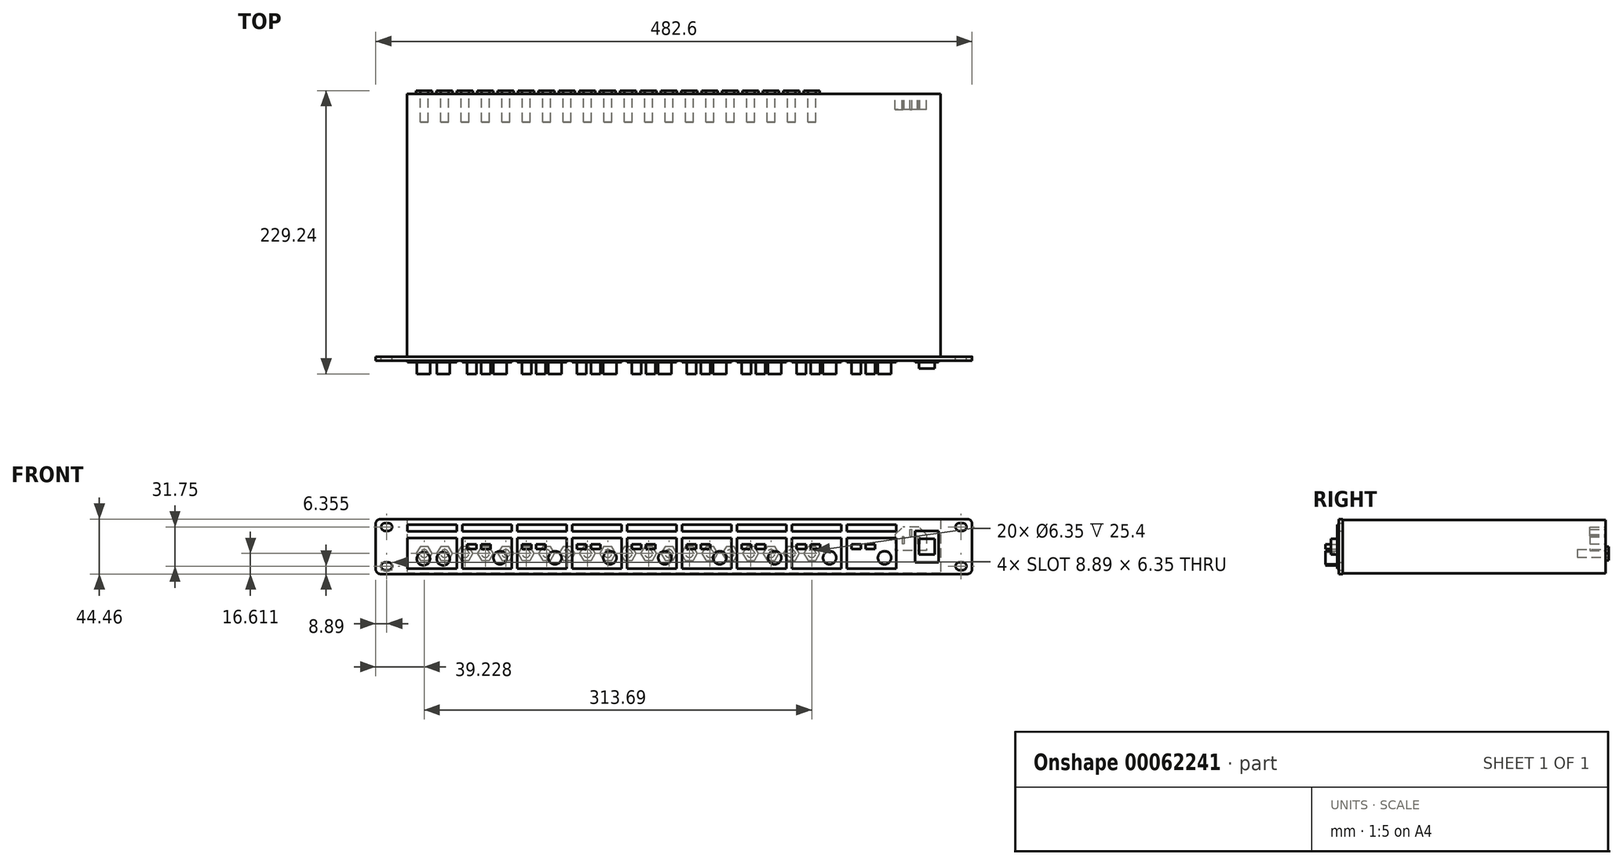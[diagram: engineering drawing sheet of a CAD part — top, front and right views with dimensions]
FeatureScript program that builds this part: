
annotation { "Feature Type Name" : "Feature", "Feature Type Description" : "" }
export const myFeature = defineFeature(function(context is Context, id is Id, definition is map)
    precondition{}
    {
        {
            var Q0;
            Q0=qCreatedBy(makeId("Front.planeOp"),FACE);
            var sketch = newSketch(context, id + "F0", { "sketchPlane" : qUnion([Q0])});
            skLineSegment(sketch, "E0.bottom", {"start": v(-237.5, 22.23) * mm, "end": v(237.5, 22.23) * mm});
            skLineSegment(sketch, "E0.top", {"start": v(-237.5, -22.22) * mm, "end": v(237.5, -22.22) * mm});
            skLineSegment(sketch, "E0.left", {"start": v(-241.3, 18.42) * mm, "end": v(-241.3, -18.41) * mm});
            skLineSegment(sketch, "E0.right", {"start": v(241.3, 18.42) * mm, "end": v(241.3, -18.42) * mm});
            skPoint(sketch, "E0.middle", {"position": v(0, 0) * mm});
            skArc(sketch, "E1", {"start": v(-233.68, 19.05) * mm, "mid": v(-236.86, 15.88) * mm, "end": v(-233.68, 12.7) * mm});
            skArc(sketch, "E2", {"start": v(-231.14, 12.7) * mm, "mid": v(-227.97, 15.88) * mm, "end": v(-231.14, 19.05) * mm});
            skLineSegment(sketch, "E3", {"start": v(-233.68, 12.7) * mm, "end": v(-231.14, 12.7) * mm});
            skLineSegment(sketch, "E4", {"start": v(-233.68, 19.05) * mm, "end": v(-231.14, 19.05) * mm});
            skPoint(sketch, "E5.visualSharp", {"position": v(-241.3, 22.23) * mm});
            skArc(sketch, "E5.filletArc", {"start": v(-237.5, 22.23) * mm, "mid": v(-240.18, 21.1) * mm, "end": v(-241.3, 18.42) * mm});
            skPoint(sketch, "E6.visualSharp", {"position": v(-241.3, -22.22) * mm});
            skArc(sketch, "E6.filletArc", {"start": v(-241.3, -18.41) * mm, "mid": v(-240.18, -21.1) * mm, "end": v(-237.5, -22.22) * mm});
            skPoint(sketch, "E7.visualSharp", {"position": v(241.3, 22.23) * mm});
            skArc(sketch, "E7.filletArc", {"start": v(241.3, 18.42) * mm, "mid": v(240.18, 21.1) * mm, "end": v(237.5, 22.23) * mm});
            skPoint(sketch, "E8.visualSharp", {"position": v(241.3, -22.22) * mm});
            skArc(sketch, "E8.filletArc", {"start": v(237.5, -22.23) * mm, "mid": v(240.18, -21.1) * mm, "end": v(241.3, -18.42) * mm});
            skLineSegment(sketch, "E9.MirrorCS", {"start": v(-233.68, -19.05) * mm, "end": v(-231.14, -19.05) * mm});
            skArc(sketch, "E10.MirrorCS", {"start": v(-231.14, -12.7) * mm, "mid": v(-227.97, -15.88) * mm, "end": v(-231.14, -19.05) * mm});
            skLineSegment(sketch, "E11.MirrorCS", {"start": v(-233.68, -12.7) * mm, "end": v(-231.14, -12.7) * mm});
            skArc(sketch, "E12.MirrorCS", {"start": v(-233.68, -19.05) * mm, "mid": v(-236.86, -15.88) * mm, "end": v(-233.68, -12.7) * mm});
            skLineSegment(sketch, "E13.MirrorCS", {"start": v(233.68, 12.7) * mm, "end": v(231.14, 12.7) * mm});
            skLineSegment(sketch, "E14.MirrorCS", {"start": v(233.68, -12.7) * mm, "end": v(231.14, -12.7) * mm});
            skLineSegment(sketch, "E15.MirrorCS", {"start": v(233.68, 19.05) * mm, "end": v(231.14, 19.05) * mm});
            skLineSegment(sketch, "E16.MirrorCS", {"start": v(233.68, -19.05) * mm, "end": v(231.14, -19.05) * mm});
            skArc(sketch, "E17.MirrorCS", {"start": v(233.68, -19.05) * mm, "mid": v(236.86, -15.88) * mm, "end": v(233.68, -12.7) * mm});
            skArc(sketch, "E18.MirrorCS", {"start": v(231.14, 12.7) * mm, "mid": v(227.97, 15.88) * mm, "end": v(231.14, 19.05) * mm});
            skArc(sketch, "E19.MirrorCS", {"start": v(233.68, 19.05) * mm, "mid": v(236.86, 15.88) * mm, "end": v(233.68, 12.7) * mm});
            skArc(sketch, "E20.MirrorCS", {"start": v(231.14, -12.7) * mm, "mid": v(227.97, -15.88) * mm, "end": v(231.14, -19.05) * mm});
            skSolve(sketch);
        }
        {
            var Q0;
            Q0=qSketchRegion(id+"F0",true);
            extrude(context, id + "F1", {"entities" : qUnion([Q0]), "depth" : 3.17 * mm});
        }
        {
            var Q0;
            Q0=makeQuery(id+"F1.opExtrude","CAP_FACE",FACE,{"disambiguationData":[OSD([sQuery(id+"F0.wireOp",EDGE,"E0.bottom"),sQuery(id+"F0.wireOp",EDGE,"E0.top"),sQuery(id+"F0.wireOp",EDGE,"E0.left"),sQuery(id+"F0.wireOp",EDGE,"E0.right"),sQuery(id+"F0.wireOp",EDGE,"E1"),sQuery(id+"F0.wireOp",EDGE,"E2"),sQuery(id+"F0.wireOp",EDGE,"E3"),sQuery(id+"F0.wireOp",EDGE,"E4"),sQuery(id+"F0.wireOp",EDGE,"E5.filletArc"),sQuery(id+"F0.wireOp",EDGE,"E6.filletArc"),sQuery(id+"F0.wireOp",EDGE,"E7.filletArc"),sQuery(id+"F0.wireOp",EDGE,"E8.filletArc"),sQuery(id+"F0.wireOp",EDGE,"E9.MirrorCS"),sQuery(id+"F0.wireOp",EDGE,"E10.MirrorCS"),sQuery(id+"F0.wireOp",EDGE,"E11.MirrorCS"),sQuery(id+"F0.wireOp",EDGE,"E12.MirrorCS"),sQuery(id+"F0.wireOp",EDGE,"E13.MirrorCS"),sQuery(id+"F0.wireOp",EDGE,"E14.MirrorCS"),sQuery(id+"F0.wireOp",EDGE,"E15.MirrorCS"),sQuery(id+"F0.wireOp",EDGE,"E16.MirrorCS"),sQuery(id+"F0.wireOp",EDGE,"E17.MirrorCS"),sQuery(id+"F0.wireOp",EDGE,"E18.MirrorCS"),sQuery(id+"F0.wireOp",EDGE,"E19.MirrorCS"),sQuery(id+"F0.wireOp",EDGE,"E20.MirrorCS")])],"isStart":true});
            var sketch = newSketch(context, id + "F2", { "sketchPlane" : qUnion([Q0])});
            skLineSegment(sketch, "E21.bottom", {"start": v(-215.9, 21.59) * mm, "end": v(215.9, 21.59) * mm});
            skLineSegment(sketch, "E21.top", {"start": v(-215.9, -21.6) * mm, "end": v(215.9, -21.6) * mm});
            skLineSegment(sketch, "E21.left", {"start": v(-215.9, 21.59) * mm, "end": v(-215.9, -21.6) * mm});
            skLineSegment(sketch, "E21.right", {"start": v(215.9, 21.59) * mm, "end": v(215.9, -21.6) * mm});
            skPoint(sketch, "E21.middle", {"position": v(0, 0) * mm});
            skSolve(sketch);
        }
        {
            var Q0;
            Q0 = qSketchRegion(id + "F2", true);
            extrude(context, id + "F3", {"entities" : qUnion([Q0]), "operationType" : NewBodyOperationType.ADD, "depth" : 212.72 * mm});
        }
        {
            var Q0;
            Q0=makeQuery(id+"F3.opExtrude","CAP_FACE",FACE,{"disambiguationData":[OSD([sQuery(id+"F2.wireOp",EDGE,"E21.bottom"),sQuery(id+"F2.wireOp",EDGE,"E21.top"),sQuery(id+"F2.wireOp",EDGE,"E21.left"),sQuery(id+"F2.wireOp",EDGE,"E21.right")])],"isStart":false});
            var sketch = newSketch(context, id + "F4", { "sketchPlane" : qUnion([Q0])});
            skCircle(sketch, "E22.cCircle", {"center": v(-111.62, -5.62) * mm, "radius": 5.62 * mm, "construction": true});
            skLineSegment(sketch, "E22.0", {"start": v(-114.86, 0) * mm, "end": v(-108.37, 0) * mm});
            skLineSegment(sketch, "E22.1", {"start": v(-108.37, 0) * mm, "end": v(-105.13, -5.62) * mm});
            skLineSegment(sketch, "E22.2", {"start": v(-105.13, -5.62) * mm, "end": v(-108.37, -11.24) * mm});
            skLineSegment(sketch, "E22.3", {"start": v(-108.37, -11.24) * mm, "end": v(-114.86, -11.24) * mm});
            skLineSegment(sketch, "E22.4", {"start": v(-114.86, -11.24) * mm, "end": v(-118.1, -5.62) * mm});
            skLineSegment(sketch, "E22.5", {"start": v(-118.1, -5.62) * mm, "end": v(-114.86, 0) * mm});
            skPoint(sketch, "E22.0.midPoint", {"position": v(-111.62, 0) * mm});
            skLineSegment(sketch, "E23.1.0.0", {"start": v(-88.62, -5.62) * mm, "end": v(-91.86, -11.24) * mm});
            skLineSegment(sketch, "E23.1.0.1", {"start": v(-91.86, 0) * mm, "end": v(-88.62, -5.62) * mm});
            skLineSegment(sketch, "E23.1.0.2", {"start": v(-98.35, 0) * mm, "end": v(-91.86, 0) * mm});
            skCircle(sketch, "E23.1.0.3", {"center": v(-95.1, -5.62) * mm, "radius": 5.62 * mm, "construction": true});
            skPoint(sketch, "E23.1.0.4", {"position": v(-95.1, 0) * mm});
            skLineSegment(sketch, "E23.1.0.5", {"start": v(-101.6, -5.62) * mm, "end": v(-98.35, 0) * mm});
            skLineSegment(sketch, "E23.1.0.6", {"start": v(-98.35, -11.24) * mm, "end": v(-101.6, -5.62) * mm});
            skLineSegment(sketch, "E23.1.0.7", {"start": v(-91.86, -11.24) * mm, "end": v(-98.35, -11.24) * mm});
            skLineSegment(sketch, "E23.2.0.0", {"start": v(-72.1, -5.62) * mm, "end": v(-75.35, -11.24) * mm});
            skLineSegment(sketch, "E23.2.0.1", {"start": v(-75.35, 0) * mm, "end": v(-72.1, -5.62) * mm});
            skLineSegment(sketch, "E23.2.0.2", {"start": v(-81.84, 0) * mm, "end": v(-75.35, 0) * mm});
            skCircle(sketch, "E23.2.0.3", {"center": v(-78.6, -5.62) * mm, "radius": 5.62 * mm, "construction": true});
            skPoint(sketch, "E23.2.0.4", {"position": v(-78.6, 0) * mm});
            skLineSegment(sketch, "E23.2.0.5", {"start": v(-85.09, -5.62) * mm, "end": v(-81.84, 0) * mm});
            skLineSegment(sketch, "E23.2.0.6", {"start": v(-81.84, -11.24) * mm, "end": v(-85.09, -5.62) * mm});
            skLineSegment(sketch, "E23.2.0.7", {"start": v(-75.35, -11.24) * mm, "end": v(-81.84, -11.24) * mm});
            skLineSegment(sketch, "E23.3.0.0", {"start": v(-55.6, -5.62) * mm, "end": v(-58.84, -11.24) * mm});
            skLineSegment(sketch, "E23.3.0.1", {"start": v(-58.84, 0) * mm, "end": v(-55.6, -5.62) * mm});
            skLineSegment(sketch, "E23.3.0.2", {"start": v(-65.33, 0) * mm, "end": v(-58.84, 0) * mm});
            skCircle(sketch, "E23.3.0.3", {"center": v(-62.09, -5.62) * mm, "radius": 5.62 * mm, "construction": true});
            skPoint(sketch, "E23.3.0.4", {"position": v(-62.09, 0) * mm});
            skLineSegment(sketch, "E23.3.0.5", {"start": v(-68.58, -5.62) * mm, "end": v(-65.33, 0) * mm});
            skLineSegment(sketch, "E23.3.0.6", {"start": v(-65.33, -11.24) * mm, "end": v(-68.58, -5.62) * mm});
            skLineSegment(sketch, "E23.3.0.7", {"start": v(-58.84, -11.24) * mm, "end": v(-65.33, -11.24) * mm});
            skLineSegment(sketch, "E23.4.0.0", {"start": v(-39.09, -5.62) * mm, "end": v(-42.33, -11.24) * mm});
            skLineSegment(sketch, "E23.4.0.1", {"start": v(-42.33, 0) * mm, "end": v(-39.09, -5.62) * mm});
            skLineSegment(sketch, "E23.4.0.2", {"start": v(-48.82, 0) * mm, "end": v(-42.33, 0) * mm});
            skCircle(sketch, "E23.4.0.3", {"center": v(-45.58, -5.62) * mm, "radius": 5.62 * mm, "construction": true});
            skPoint(sketch, "E23.4.0.4", {"position": v(-45.58, 0) * mm});
            skLineSegment(sketch, "E23.4.0.5", {"start": v(-52.07, -5.62) * mm, "end": v(-48.82, 0) * mm});
            skLineSegment(sketch, "E23.4.0.6", {"start": v(-48.82, -11.24) * mm, "end": v(-52.07, -5.62) * mm});
            skLineSegment(sketch, "E23.4.0.7", {"start": v(-42.33, -11.24) * mm, "end": v(-48.82, -11.24) * mm});
            skLineSegment(sketch, "E23.5.0.0", {"start": v(-22.58, -5.62) * mm, "end": v(-25.82, -11.24) * mm});
            skLineSegment(sketch, "E23.5.0.1", {"start": v(-25.82, 0) * mm, "end": v(-22.58, -5.62) * mm});
            skLineSegment(sketch, "E23.5.0.2", {"start": v(-32.31, 0) * mm, "end": v(-25.82, 0) * mm});
            skCircle(sketch, "E23.5.0.3", {"center": v(-29.07, -5.62) * mm, "radius": 5.62 * mm, "construction": true});
            skPoint(sketch, "E23.5.0.4", {"position": v(-29.07, 0) * mm});
            skLineSegment(sketch, "E23.5.0.5", {"start": v(-35.56, -5.62) * mm, "end": v(-32.31, 0) * mm});
            skLineSegment(sketch, "E23.5.0.6", {"start": v(-32.31, -11.24) * mm, "end": v(-35.56, -5.62) * mm});
            skLineSegment(sketch, "E23.5.0.7", {"start": v(-25.82, -11.24) * mm, "end": v(-32.31, -11.24) * mm});
            skLineSegment(sketch, "E23.6.0.0", {"start": v(-6.07, -5.62) * mm, "end": v(-9.31, -11.24) * mm});
            skLineSegment(sketch, "E23.6.0.1", {"start": v(-9.31, 0) * mm, "end": v(-6.07, -5.62) * mm});
            skLineSegment(sketch, "E23.6.0.2", {"start": v(-15.8, 0) * mm, "end": v(-9.31, 0) * mm});
            skCircle(sketch, "E23.6.0.3", {"center": v(-12.56, -5.62) * mm, "radius": 5.62 * mm, "construction": true});
            skPoint(sketch, "E23.6.0.4", {"position": v(-12.56, 0) * mm});
            skLineSegment(sketch, "E23.6.0.5", {"start": v(-19.05, -5.62) * mm, "end": v(-15.8, 0) * mm});
            skLineSegment(sketch, "E23.6.0.6", {"start": v(-15.8, -11.24) * mm, "end": v(-19.05, -5.62) * mm});
            skLineSegment(sketch, "E23.6.0.7", {"start": v(-9.31, -11.24) * mm, "end": v(-15.8, -11.24) * mm});
            skLineSegment(sketch, "E23.7.0.0", {"start": v(10.44, -5.62) * mm, "end": v(7.2, -11.24) * mm});
            skLineSegment(sketch, "E23.7.0.1", {"start": v(7.2, 0) * mm, "end": v(10.44, -5.62) * mm});
            skLineSegment(sketch, "E23.7.0.2", {"start": v(0.7, 0) * mm, "end": v(7.2, 0) * mm});
            skCircle(sketch, "E23.7.0.3", {"center": v(3.95, -5.62) * mm, "radius": 5.62 * mm, "construction": true});
            skPoint(sketch, "E23.7.0.4", {"position": v(3.95, 0) * mm});
            skLineSegment(sketch, "E23.7.0.5", {"start": v(-2.54, -5.62) * mm, "end": v(0.7, 0) * mm});
            skLineSegment(sketch, "E23.7.0.6", {"start": v(0.7, -11.24) * mm, "end": v(-2.54, -5.62) * mm});
            skLineSegment(sketch, "E23.7.0.7", {"start": v(7.2, -11.24) * mm, "end": v(0.7, -11.24) * mm});
            skLineSegment(sketch, "E23.8.0.0", {"start": v(26.95, -5.62) * mm, "end": v(23.7, -11.24) * mm});
            skLineSegment(sketch, "E23.8.0.1", {"start": v(23.7, 0) * mm, "end": v(26.95, -5.62) * mm});
            skLineSegment(sketch, "E23.8.0.2", {"start": v(17.22, 0) * mm, "end": v(23.7, 0) * mm});
            skCircle(sketch, "E23.8.0.3", {"center": v(20.46, -5.62) * mm, "radius": 5.62 * mm, "construction": true});
            skPoint(sketch, "E23.8.0.4", {"position": v(20.46, 0) * mm});
            skLineSegment(sketch, "E23.8.0.5", {"start": v(13.97, -5.62) * mm, "end": v(17.22, 0) * mm});
            skLineSegment(sketch, "E23.8.0.6", {"start": v(17.22, -11.24) * mm, "end": v(13.97, -5.62) * mm});
            skLineSegment(sketch, "E23.8.0.7", {"start": v(23.7, -11.24) * mm, "end": v(17.22, -11.24) * mm});
            skLineSegment(sketch, "E23.9.0.0", {"start": v(43.46, -5.62) * mm, "end": v(40.22, -11.24) * mm});
            skLineSegment(sketch, "E23.9.0.1", {"start": v(40.22, 0) * mm, "end": v(43.46, -5.62) * mm});
            skLineSegment(sketch, "E23.9.0.2", {"start": v(33.73, 0) * mm, "end": v(40.22, 0) * mm});
            skCircle(sketch, "E23.9.0.3", {"center": v(36.97, -5.62) * mm, "radius": 5.62 * mm, "construction": true});
            skPoint(sketch, "E23.9.0.4", {"position": v(36.97, 0) * mm});
            skLineSegment(sketch, "E23.9.0.5", {"start": v(30.48, -5.62) * mm, "end": v(33.73, 0) * mm});
            skLineSegment(sketch, "E23.9.0.6", {"start": v(33.73, -11.24) * mm, "end": v(30.48, -5.62) * mm});
            skLineSegment(sketch, "E23.9.0.7", {"start": v(40.22, -11.24) * mm, "end": v(33.73, -11.24) * mm});
            skLineSegment(sketch, "E23.10.0.0", {"start": v(59.97, -5.62) * mm, "end": v(56.73, -11.24) * mm});
            skLineSegment(sketch, "E23.10.0.1", {"start": v(56.73, 0) * mm, "end": v(59.97, -5.62) * mm});
            skLineSegment(sketch, "E23.10.0.2", {"start": v(50.24, 0) * mm, "end": v(56.73, 0) * mm});
            skCircle(sketch, "E23.10.0.3", {"center": v(53.48, -5.62) * mm, "radius": 5.62 * mm, "construction": true});
            skPoint(sketch, "E23.10.0.4", {"position": v(53.48, 0) * mm});
            skLineSegment(sketch, "E23.10.0.5", {"start": v(47, -5.62) * mm, "end": v(50.24, 0) * mm});
            skLineSegment(sketch, "E23.10.0.6", {"start": v(50.24, -11.24) * mm, "end": v(47, -5.62) * mm});
            skLineSegment(sketch, "E23.10.0.7", {"start": v(56.73, -11.24) * mm, "end": v(50.24, -11.24) * mm});
            skLineSegment(sketch, "E23.11.0.0", {"start": v(76.48, -5.62) * mm, "end": v(73.24, -11.24) * mm});
            skLineSegment(sketch, "E23.11.0.1", {"start": v(73.24, 0) * mm, "end": v(76.48, -5.62) * mm});
            skLineSegment(sketch, "E23.11.0.2", {"start": v(66.75, 0) * mm, "end": v(73.24, 0) * mm});
            skCircle(sketch, "E23.11.0.3", {"center": v(70, -5.62) * mm, "radius": 5.62 * mm, "construction": true});
            skPoint(sketch, "E23.11.0.4", {"position": v(70, 0) * mm});
            skLineSegment(sketch, "E23.11.0.5", {"start": v(63.5, -5.62) * mm, "end": v(66.75, 0) * mm});
            skLineSegment(sketch, "E23.11.0.6", {"start": v(66.75, -11.24) * mm, "end": v(63.5, -5.62) * mm});
            skLineSegment(sketch, "E23.11.0.7", {"start": v(73.24, -11.24) * mm, "end": v(66.75, -11.24) * mm});
            skLineSegment(sketch, "E23.12.0.0", {"start": v(93, -5.62) * mm, "end": v(89.75, -11.24) * mm});
            skLineSegment(sketch, "E23.12.0.1", {"start": v(89.75, 0) * mm, "end": v(93, -5.62) * mm});
            skLineSegment(sketch, "E23.12.0.2", {"start": v(83.26, 0) * mm, "end": v(89.75, 0) * mm});
            skCircle(sketch, "E23.12.0.3", {"center": v(86.5, -5.62) * mm, "radius": 5.62 * mm, "construction": true});
            skPoint(sketch, "E23.12.0.4", {"position": v(86.5, 0) * mm});
            skLineSegment(sketch, "E23.12.0.5", {"start": v(80.01, -5.62) * mm, "end": v(83.26, 0) * mm});
            skLineSegment(sketch, "E23.12.0.6", {"start": v(83.26, -11.24) * mm, "end": v(80.01, -5.62) * mm});
            skLineSegment(sketch, "E23.12.0.7", {"start": v(89.75, -11.24) * mm, "end": v(83.26, -11.24) * mm});
            skLineSegment(sketch, "E23.13.0.0", {"start": v(109.5, -5.62) * mm, "end": v(106.26, -11.24) * mm});
            skLineSegment(sketch, "E23.13.0.1", {"start": v(106.26, 0) * mm, "end": v(109.5, -5.62) * mm});
            skLineSegment(sketch, "E23.13.0.2", {"start": v(99.77, 0) * mm, "end": v(106.26, 0) * mm});
            skCircle(sketch, "E23.13.0.3", {"center": v(103.01, -5.62) * mm, "radius": 5.62 * mm, "construction": true});
            skPoint(sketch, "E23.13.0.4", {"position": v(103.01, 0) * mm});
            skLineSegment(sketch, "E23.13.0.5", {"start": v(96.52, -5.62) * mm, "end": v(99.77, 0) * mm});
            skLineSegment(sketch, "E23.13.0.6", {"start": v(99.77, -11.24) * mm, "end": v(96.52, -5.62) * mm});
            skLineSegment(sketch, "E23.13.0.7", {"start": v(106.26, -11.24) * mm, "end": v(99.77, -11.24) * mm});
            skLineSegment(sketch, "E23.14.0.0", {"start": v(126.01, -5.62) * mm, "end": v(122.77, -11.24) * mm});
            skLineSegment(sketch, "E23.14.0.1", {"start": v(122.77, 0) * mm, "end": v(126.01, -5.62) * mm});
            skLineSegment(sketch, "E23.14.0.2", {"start": v(116.28, 0) * mm, "end": v(122.77, 0) * mm});
            skCircle(sketch, "E23.14.0.3", {"center": v(119.52, -5.62) * mm, "radius": 5.62 * mm, "construction": true});
            skPoint(sketch, "E23.14.0.4", {"position": v(119.52, 0) * mm});
            skLineSegment(sketch, "E23.14.0.5", {"start": v(113.03, -5.62) * mm, "end": v(116.28, 0) * mm});
            skLineSegment(sketch, "E23.14.0.6", {"start": v(116.28, -11.24) * mm, "end": v(113.03, -5.62) * mm});
            skLineSegment(sketch, "E23.14.0.7", {"start": v(122.77, -11.24) * mm, "end": v(116.28, -11.24) * mm});
            skLineSegment(sketch, "E23.15.0.0", {"start": v(142.52, -5.62) * mm, "end": v(139.28, -11.24) * mm});
            skLineSegment(sketch, "E23.15.0.1", {"start": v(139.28, 0) * mm, "end": v(142.52, -5.62) * mm});
            skLineSegment(sketch, "E23.15.0.2", {"start": v(132.79, 0) * mm, "end": v(139.28, 0) * mm});
            skCircle(sketch, "E23.15.0.3", {"center": v(136.03, -5.62) * mm, "radius": 5.62 * mm, "construction": true});
            skPoint(sketch, "E23.15.0.4", {"position": v(136.03, 0) * mm});
            skLineSegment(sketch, "E23.15.0.5", {"start": v(129.54, -5.62) * mm, "end": v(132.79, 0) * mm});
            skLineSegment(sketch, "E23.15.0.6", {"start": v(132.79, -11.24) * mm, "end": v(129.54, -5.62) * mm});
            skLineSegment(sketch, "E23.15.0.7", {"start": v(139.28, -11.24) * mm, "end": v(132.79, -11.24) * mm});
            skLineSegment(sketch, "E23.16.0.0", {"start": v(159.03, -5.62) * mm, "end": v(155.79, -11.24) * mm});
            skLineSegment(sketch, "E23.16.0.1", {"start": v(155.79, 0) * mm, "end": v(159.03, -5.62) * mm});
            skLineSegment(sketch, "E23.16.0.2", {"start": v(149.3, 0) * mm, "end": v(155.79, 0) * mm});
            skCircle(sketch, "E23.16.0.3", {"center": v(152.54, -5.62) * mm, "radius": 5.62 * mm, "construction": true});
            skPoint(sketch, "E23.16.0.4", {"position": v(152.54, 0) * mm});
            skLineSegment(sketch, "E23.16.0.5", {"start": v(146.05, -5.62) * mm, "end": v(149.3, 0) * mm});
            skLineSegment(sketch, "E23.16.0.6", {"start": v(149.3, -11.24) * mm, "end": v(146.05, -5.62) * mm});
            skLineSegment(sketch, "E23.16.0.7", {"start": v(155.79, -11.24) * mm, "end": v(149.3, -11.24) * mm});
            skLineSegment(sketch, "E23.17.0.0", {"start": v(175.54, -5.62) * mm, "end": v(172.3, -11.24) * mm});
            skLineSegment(sketch, "E23.17.0.1", {"start": v(172.3, 0) * mm, "end": v(175.54, -5.62) * mm});
            skLineSegment(sketch, "E23.17.0.2", {"start": v(165.8, 0) * mm, "end": v(172.3, 0) * mm});
            skCircle(sketch, "E23.17.0.3", {"center": v(169.05, -5.62) * mm, "radius": 5.62 * mm, "construction": true});
            skPoint(sketch, "E23.17.0.4", {"position": v(169.05, 0) * mm});
            skLineSegment(sketch, "E23.17.0.5", {"start": v(162.56, -5.62) * mm, "end": v(165.8, 0) * mm});
            skLineSegment(sketch, "E23.17.0.6", {"start": v(165.8, -11.24) * mm, "end": v(162.56, -5.62) * mm});
            skLineSegment(sketch, "E23.17.0.7", {"start": v(172.3, -11.24) * mm, "end": v(165.8, -11.24) * mm});
            skLineSegment(sketch, "E23.18.0.0", {"start": v(192.05, -5.62) * mm, "end": v(188.8, -11.24) * mm});
            skLineSegment(sketch, "E23.18.0.1", {"start": v(188.8, 0) * mm, "end": v(192.05, -5.62) * mm});
            skLineSegment(sketch, "E23.18.0.2", {"start": v(182.32, 0) * mm, "end": v(188.8, 0) * mm});
            skCircle(sketch, "E23.18.0.3", {"center": v(185.56, -5.62) * mm, "radius": 5.62 * mm, "construction": true});
            skPoint(sketch, "E23.18.0.4", {"position": v(185.56, 0) * mm});
            skLineSegment(sketch, "E23.18.0.5", {"start": v(179.07, -5.62) * mm, "end": v(182.32, 0) * mm});
            skLineSegment(sketch, "E23.18.0.6", {"start": v(182.32, -11.24) * mm, "end": v(179.07, -5.62) * mm});
            skLineSegment(sketch, "E23.18.0.7", {"start": v(188.8, -11.24) * mm, "end": v(182.32, -11.24) * mm});
            skLineSegment(sketch, "E23.19.0.0", {"start": v(208.56, -5.62) * mm, "end": v(205.32, -11.24) * mm});
            skLineSegment(sketch, "E23.19.0.1", {"start": v(205.32, 0) * mm, "end": v(208.56, -5.62) * mm});
            skLineSegment(sketch, "E23.19.0.2", {"start": v(198.83, 0) * mm, "end": v(205.32, 0) * mm});
            skCircle(sketch, "E23.19.0.3", {"center": v(202.07, -5.62) * mm, "radius": 5.62 * mm, "construction": true});
            skPoint(sketch, "E23.19.0.4", {"position": v(202.07, 0) * mm});
            skLineSegment(sketch, "E23.19.0.5", {"start": v(195.58, -5.62) * mm, "end": v(198.83, 0) * mm});
            skLineSegment(sketch, "E23.19.0.6", {"start": v(198.83, -11.24) * mm, "end": v(195.58, -5.62) * mm});
            skLineSegment(sketch, "E23.19.0.7", {"start": v(205.32, -11.24) * mm, "end": v(198.83, -11.24) * mm});
            skLineSegment(sketch, "E23.direction1", {"start": v(-108.37, -11.24) * mm, "end": v(-91.86, -11.24) * mm, "construction": true});
            skSolve(sketch);
        }
        {
            var Q0;
            Q0 = qSketchRegion(id + "F4", true);
            extrude(context, id + "F5", {"entities" : qUnion([Q0]), "operationType" : NewBodyOperationType.ADD, "depth" : 2.54 * mm});
        }
        {
            var Q0;
            Q0=makeQuery(id+"F5.opExtrude","CAP_FACE",FACE,{"disambiguationData":[OSD([sQuery(id+"F4.wireOp",EDGE,"E22.0"),sQuery(id+"F4.wireOp",EDGE,"E22.1"),sQuery(id+"F4.wireOp",EDGE,"E22.2"),sQuery(id+"F4.wireOp",EDGE,"E22.3"),sQuery(id+"F4.wireOp",EDGE,"E22.4"),sQuery(id+"F4.wireOp",EDGE,"E22.5")])],"isStart":false});
            var sketch = newSketch(context, id + "F6", { "sketchPlane" : qUnion([Q0])});
            skCircle(sketch, "E24", {"center": v(-111.62, -5.62) * mm, "radius": 3.18 * mm});
            skPoint(sketch, "E24.centerSnap0", {"position": v(-111.62, 0) * mm});
            skCircle(sketch, "E25.1.0.0", {"center": v(-95.1, -5.62) * mm, "radius": 3.18 * mm});
            skCircle(sketch, "E25.2.0.0", {"center": v(-78.6, -5.62) * mm, "radius": 3.18 * mm});
            skCircle(sketch, "E25.3.0.0", {"center": v(-62.09, -5.62) * mm, "radius": 3.18 * mm});
            skCircle(sketch, "E25.4.0.0", {"center": v(-45.58, -5.62) * mm, "radius": 3.18 * mm});
            skCircle(sketch, "E25.5.0.0", {"center": v(-29.07, -5.62) * mm, "radius": 3.18 * mm});
            skCircle(sketch, "E25.6.0.0", {"center": v(-12.56, -5.62) * mm, "radius": 3.18 * mm});
            skCircle(sketch, "E25.7.0.0", {"center": v(3.95, -5.62) * mm, "radius": 3.18 * mm});
            skCircle(sketch, "E25.8.0.0", {"center": v(20.46, -5.62) * mm, "radius": 3.18 * mm});
            skCircle(sketch, "E25.9.0.0", {"center": v(36.97, -5.62) * mm, "radius": 3.18 * mm});
            skCircle(sketch, "E25.10.0.0", {"center": v(53.48, -5.62) * mm, "radius": 3.18 * mm});
            skCircle(sketch, "E25.11.0.0", {"center": v(70, -5.62) * mm, "radius": 3.18 * mm});
            skCircle(sketch, "E25.12.0.0", {"center": v(86.5, -5.62) * mm, "radius": 3.18 * mm});
            skCircle(sketch, "E25.13.0.0", {"center": v(103.01, -5.62) * mm, "radius": 3.18 * mm});
            skCircle(sketch, "E25.14.0.0", {"center": v(119.52, -5.62) * mm, "radius": 3.18 * mm});
            skCircle(sketch, "E25.15.0.0", {"center": v(136.03, -5.62) * mm, "radius": 3.18 * mm});
            skCircle(sketch, "E25.16.0.0", {"center": v(152.54, -5.62) * mm, "radius": 3.18 * mm});
            skCircle(sketch, "E25.17.0.0", {"center": v(169.05, -5.62) * mm, "radius": 3.18 * mm});
            skCircle(sketch, "E25.18.0.0", {"center": v(185.56, -5.62) * mm, "radius": 3.18 * mm});
            skCircle(sketch, "E25.19.0.0", {"center": v(202.07, -5.62) * mm, "radius": 3.18 * mm});
            skLineSegment(sketch, "E25.direction1", {"start": v(-111.62, -5.62) * mm, "end": v(-95.1, -5.62) * mm, "construction": true});
            skSolve(sketch);
        }
        {
            var Q0;
            Q0 = qSketchRegion(id + "F6", true);
            extrude(context, id + "F7", {"entities" : qUnion([Q0]), "operationType" : NewBodyOperationType.REMOVE, "oppositeDirection" : true, "depth" : 25.4 * mm});
        }
        {
            var Q0;
            Q0 = qSketchRegion(id + "F6", true);
            extrude(context, id + "F8", {"entities" : qUnion([Q0]), "operationType" : NewBodyOperationType.REMOVE, "oppositeDirection" : true, "depth" : 25.4 * mm});
        }
        {
            var Q0;
            Q0=makeQuery(id+"F3.opExtrude","CAP_FACE",FACE,{"disambiguationData":[OSD([sQuery(id+"F2.wireOp",EDGE,"E21.bottom"),sQuery(id+"F2.wireOp",EDGE,"E21.top"),sQuery(id+"F2.wireOp",EDGE,"E21.left"),sQuery(id+"F2.wireOp",EDGE,"E21.right")])],"isStart":false});
            var sketch = newSketch(context, id + "F9", { "sketchPlane" : qUnion([Q0])});
            skLineSegment(sketch, "E26.bottom", {"start": v(-198.3, 15.89) * mm, "end": v(-185.49, 15.89) * mm});
            skLineSegment(sketch, "E26.top", {"start": v(-204.48, -3.16) * mm, "end": v(-179.08, -3.16) * mm});
            skLineSegment(sketch, "E26.left", {"start": v(-204.48, 9.8) * mm, "end": v(-204.48, -3.16) * mm});
            skLineSegment(sketch, "E26.right", {"start": v(-179.08, 9.8) * mm, "end": v(-179.08, -3.16) * mm});
            skPoint(sketch, "E26.middle", {"position": v(-191.78, 6.36) * mm});
            skLineSegment(sketch, "E27", {"start": v(-204.48, 9.8) * mm, "end": v(-198.3, 15.89) * mm});
            skLineSegment(sketch, "E28", {"start": v(-179.08, 9.8) * mm, "end": v(-185.49, 15.89) * mm});
            skPoint(sketch, "E29.orphan", {"position": v(-179.08, 15.89) * mm});
            skPoint(sketch, "E30.orphan", {"position": v(-204.48, 15.89) * mm});
            skLineSegment(sketch, "E31.bottom", {"start": v(-190.98, 8.42) * mm, "end": v(-192.58, 8.42) * mm});
            skLineSegment(sketch, "E31.top", {"start": v(-190.98, 13.8) * mm, "end": v(-192.58, 13.8) * mm});
            skLineSegment(sketch, "E31.left", {"start": v(-190.98, 8.42) * mm, "end": v(-190.98, 13.8) * mm});
            skLineSegment(sketch, "E31.right", {"start": v(-192.58, 8.42) * mm, "end": v(-192.58, 13.8) * mm});
            skPoint(sketch, "E31.middle", {"position": v(-191.78, 11.12) * mm});
            skLineSegment(sketch, "E32.bottom", {"start": v(-199, 7.88) * mm, "end": v(-197.24, 7.88) * mm});
            skLineSegment(sketch, "E32.top", {"start": v(-199, 2.1) * mm, "end": v(-197.24, 2.1) * mm});
            skLineSegment(sketch, "E32.left", {"start": v(-199, 7.88) * mm, "end": v(-199, 2.1) * mm});
            skLineSegment(sketch, "E32.right", {"start": v(-197.24, 7.88) * mm, "end": v(-197.24, 2.1) * mm});
            skPoint(sketch, "E32.middle", {"position": v(-198.12, 4.99) * mm});
            skLineSegment(sketch, "E33.bottom", {"start": v(-186.4, 7.88) * mm, "end": v(-184.57, 7.88) * mm});
            skLineSegment(sketch, "E33.top", {"start": v(-186.4, 2.1) * mm, "end": v(-184.57, 2.1) * mm});
            skLineSegment(sketch, "E33.left", {"start": v(-186.4, 7.88) * mm, "end": v(-186.4, 2.1) * mm});
            skLineSegment(sketch, "E33.right", {"start": v(-184.57, 7.88) * mm, "end": v(-184.57, 2.1) * mm});
            skPoint(sketch, "E33.middle", {"position": v(-185.49, 4.99) * mm});
            skPoint(sketch, "E33.middle.positionSnap0", {"position": v(-197.24, 4.99) * mm});
            skPoint(sketch, "E33.centerSnap0", {"position": v(-197.24, 4.99) * mm});
            skSolve(sketch);
        }
        {
            var Q0;
            Q0 = qSketchRegion(id + "F9", true);
            extrude(context, id + "F10", {"entities" : qUnion([Q0]), "operationType" : NewBodyOperationType.REMOVE, "oppositeDirection" : true, "depth" : 12.7 * mm});
        }
        {
            var Q0;
            Q0=makeQuery(id+"F1.opExtrude","CAP_FACE",FACE,{"disambiguationData":[OSD([sQuery(id+"F0.wireOp",EDGE,"E0.bottom"),sQuery(id+"F0.wireOp",EDGE,"E0.top"),sQuery(id+"F0.wireOp",EDGE,"E0.left"),sQuery(id+"F0.wireOp",EDGE,"E0.right"),sQuery(id+"F0.wireOp",EDGE,"E1"),sQuery(id+"F0.wireOp",EDGE,"E2"),sQuery(id+"F0.wireOp",EDGE,"E3"),sQuery(id+"F0.wireOp",EDGE,"E4"),sQuery(id+"F0.wireOp",EDGE,"E5.filletArc"),sQuery(id+"F0.wireOp",EDGE,"E6.filletArc"),sQuery(id+"F0.wireOp",EDGE,"E7.filletArc"),sQuery(id+"F0.wireOp",EDGE,"E8.filletArc"),sQuery(id+"F0.wireOp",EDGE,"E9.MirrorCS"),sQuery(id+"F0.wireOp",EDGE,"E10.MirrorCS"),sQuery(id+"F0.wireOp",EDGE,"E11.MirrorCS"),sQuery(id+"F0.wireOp",EDGE,"E12.MirrorCS"),sQuery(id+"F0.wireOp",EDGE,"E13.MirrorCS"),sQuery(id+"F0.wireOp",EDGE,"E14.MirrorCS"),sQuery(id+"F0.wireOp",EDGE,"E15.MirrorCS"),sQuery(id+"F0.wireOp",EDGE,"E16.MirrorCS"),sQuery(id+"F0.wireOp",EDGE,"E17.MirrorCS"),sQuery(id+"F0.wireOp",EDGE,"E18.MirrorCS"),sQuery(id+"F0.wireOp",EDGE,"E19.MirrorCS"),sQuery(id+"F0.wireOp",EDGE,"E20.MirrorCS")])],"isStart":false});
            var sketch = newSketch(context, id + "F11", { "sketchPlane" : qUnion([Q0])});
            skLineSegment(sketch, "E34.bottom", {"start": v(-215.61, 7.05) * mm, "end": v(-175.61, 7.05) * mm});
            skLineSegment(sketch, "E34.top", {"start": v(-215.61, -17.71) * mm, "end": v(-175.61, -17.71) * mm});
            skLineSegment(sketch, "E34.left", {"start": v(-215.61, 7.05) * mm, "end": v(-215.61, -17.71) * mm});
            skLineSegment(sketch, "E34.right", {"start": v(-175.61, 7.05) * mm, "end": v(-175.61, -17.71) * mm});
            skPoint(sketch, "E34.middle", {"position": v(-195.61, -5.33) * mm});
            skLineSegment(sketch, "E35.bottom", {"start": v(-175.61, 12.38) * mm, "end": v(-215.61, 12.38) * mm});
            skLineSegment(sketch, "E35.top", {"start": v(-175.61, 17.71) * mm, "end": v(-215.61, 17.71) * mm});
            skLineSegment(sketch, "E35.left", {"start": v(-175.61, 12.38) * mm, "end": v(-175.61, 17.71) * mm});
            skLineSegment(sketch, "E35.right", {"start": v(-215.61, 12.38) * mm, "end": v(-215.61, 17.71) * mm});
            skPoint(sketch, "E35.middle", {"position": v(-195.61, 15.05) * mm});
            skPoint(sketch, "E35.middle.positionSnap0", {"position": v(-195.61, 7.05) * mm});
            skPoint(sketch, "E35.centerSnap0", {"position": v(-195.61, 7.05) * mm});
            skLineSegment(sketch, "E36.1.0.0", {"start": v(-171.16, -17.71) * mm, "end": v(-131.16, -17.71) * mm});
            skLineSegment(sketch, "E36.1.0.1", {"start": v(-171.16, 7.05) * mm, "end": v(-171.16, -17.71) * mm});
            skLineSegment(sketch, "E36.1.0.2", {"start": v(-131.16, 7.05) * mm, "end": v(-131.16, -17.71) * mm});
            skPoint(sketch, "E36.1.0.3", {"position": v(-151.16, -5.33) * mm});
            skPoint(sketch, "E36.1.0.4", {"position": v(-151.16, 7.05) * mm});
            skLineSegment(sketch, "E36.1.0.5", {"start": v(-171.16, 7.05) * mm, "end": v(-131.16, 7.05) * mm});
            skLineSegment(sketch, "E36.1.0.6", {"start": v(-131.16, 12.38) * mm, "end": v(-171.16, 12.38) * mm});
            skPoint(sketch, "E36.1.0.7", {"position": v(-151.16, 15.05) * mm});
            skLineSegment(sketch, "E36.1.0.8", {"start": v(-131.16, 17.71) * mm, "end": v(-171.16, 17.71) * mm});
            skPoint(sketch, "E36.1.0.9", {"position": v(-151.16, 7.05) * mm});
            skLineSegment(sketch, "E36.1.0.10", {"start": v(-171.16, 12.38) * mm, "end": v(-171.16, 17.71) * mm});
            skLineSegment(sketch, "E36.1.0.11", {"start": v(-131.16, 12.38) * mm, "end": v(-131.16, 17.71) * mm});
            skLineSegment(sketch, "E36.2.0.0", {"start": v(-126.71, -17.71) * mm, "end": v(-86.71, -17.71) * mm});
            skLineSegment(sketch, "E36.2.0.1", {"start": v(-126.71, 7.05) * mm, "end": v(-126.71, -17.71) * mm});
            skLineSegment(sketch, "E36.2.0.2", {"start": v(-86.71, 7.05) * mm, "end": v(-86.71, -17.71) * mm});
            skPoint(sketch, "E36.2.0.3", {"position": v(-106.71, -5.33) * mm});
            skPoint(sketch, "E36.2.0.4", {"position": v(-106.71, 7.05) * mm});
            skLineSegment(sketch, "E36.2.0.5", {"start": v(-126.71, 7.05) * mm, "end": v(-86.71, 7.05) * mm});
            skLineSegment(sketch, "E36.2.0.6", {"start": v(-86.71, 12.38) * mm, "end": v(-126.71, 12.38) * mm});
            skPoint(sketch, "E36.2.0.7", {"position": v(-106.71, 15.05) * mm});
            skLineSegment(sketch, "E36.2.0.8", {"start": v(-86.71, 17.71) * mm, "end": v(-126.71, 17.71) * mm});
            skPoint(sketch, "E36.2.0.9", {"position": v(-106.71, 7.05) * mm});
            skLineSegment(sketch, "E36.2.0.10", {"start": v(-126.71, 12.38) * mm, "end": v(-126.71, 17.71) * mm});
            skLineSegment(sketch, "E36.2.0.11", {"start": v(-86.71, 12.38) * mm, "end": v(-86.71, 17.71) * mm});
            skLineSegment(sketch, "E36.3.0.0", {"start": v(-82.26, -17.71) * mm, "end": v(-42.26, -17.71) * mm});
            skLineSegment(sketch, "E36.3.0.1", {"start": v(-82.26, 7.05) * mm, "end": v(-82.26, -17.71) * mm});
            skLineSegment(sketch, "E36.3.0.2", {"start": v(-42.26, 7.05) * mm, "end": v(-42.26, -17.71) * mm});
            skPoint(sketch, "E36.3.0.3", {"position": v(-62.26, -5.33) * mm});
            skPoint(sketch, "E36.3.0.4", {"position": v(-62.26, 7.05) * mm});
            skLineSegment(sketch, "E36.3.0.5", {"start": v(-82.26, 7.05) * mm, "end": v(-42.26, 7.05) * mm});
            skLineSegment(sketch, "E36.3.0.6", {"start": v(-42.26, 12.38) * mm, "end": v(-82.26, 12.38) * mm});
            skPoint(sketch, "E36.3.0.7", {"position": v(-62.26, 15.05) * mm});
            skLineSegment(sketch, "E36.3.0.8", {"start": v(-42.26, 17.71) * mm, "end": v(-82.26, 17.71) * mm});
            skPoint(sketch, "E36.3.0.9", {"position": v(-62.26, 7.05) * mm});
            skLineSegment(sketch, "E36.3.0.10", {"start": v(-82.26, 12.38) * mm, "end": v(-82.26, 17.71) * mm});
            skLineSegment(sketch, "E36.3.0.11", {"start": v(-42.26, 12.38) * mm, "end": v(-42.26, 17.71) * mm});
            skLineSegment(sketch, "E36.4.0.0", {"start": v(-37.81, -17.71) * mm, "end": v(2.19, -17.71) * mm});
            skLineSegment(sketch, "E36.4.0.1", {"start": v(-37.81, 7.05) * mm, "end": v(-37.81, -17.71) * mm});
            skLineSegment(sketch, "E36.4.0.2", {"start": v(2.19, 7.05) * mm, "end": v(2.19, -17.71) * mm});
            skPoint(sketch, "E36.4.0.3", {"position": v(-17.81, -5.33) * mm});
            skPoint(sketch, "E36.4.0.4", {"position": v(-17.81, 7.05) * mm});
            skLineSegment(sketch, "E36.4.0.5", {"start": v(-37.81, 7.05) * mm, "end": v(2.19, 7.05) * mm});
            skLineSegment(sketch, "E36.4.0.6", {"start": v(2.19, 12.38) * mm, "end": v(-37.81, 12.38) * mm});
            skPoint(sketch, "E36.4.0.7", {"position": v(-17.81, 15.05) * mm});
            skLineSegment(sketch, "E36.4.0.8", {"start": v(2.19, 17.71) * mm, "end": v(-37.81, 17.71) * mm});
            skPoint(sketch, "E36.4.0.9", {"position": v(-17.81, 7.05) * mm});
            skLineSegment(sketch, "E36.4.0.10", {"start": v(-37.81, 12.38) * mm, "end": v(-37.81, 17.71) * mm});
            skLineSegment(sketch, "E36.4.0.11", {"start": v(2.19, 12.38) * mm, "end": v(2.19, 17.71) * mm});
            skLineSegment(sketch, "E36.5.0.0", {"start": v(6.64, -17.71) * mm, "end": v(46.64, -17.71) * mm});
            skLineSegment(sketch, "E36.5.0.1", {"start": v(6.64, 7.05) * mm, "end": v(6.64, -17.71) * mm});
            skLineSegment(sketch, "E36.5.0.2", {"start": v(46.64, 7.05) * mm, "end": v(46.64, -17.71) * mm});
            skPoint(sketch, "E36.5.0.3", {"position": v(26.64, -5.33) * mm});
            skPoint(sketch, "E36.5.0.4", {"position": v(26.64, 7.05) * mm});
            skLineSegment(sketch, "E36.5.0.5", {"start": v(6.64, 7.05) * mm, "end": v(46.64, 7.05) * mm});
            skLineSegment(sketch, "E36.5.0.6", {"start": v(46.64, 12.38) * mm, "end": v(6.64, 12.38) * mm});
            skPoint(sketch, "E36.5.0.7", {"position": v(26.64, 15.05) * mm});
            skLineSegment(sketch, "E36.5.0.8", {"start": v(46.64, 17.71) * mm, "end": v(6.64, 17.71) * mm});
            skPoint(sketch, "E36.5.0.9", {"position": v(26.64, 7.05) * mm});
            skLineSegment(sketch, "E36.5.0.10", {"start": v(6.64, 12.38) * mm, "end": v(6.64, 17.71) * mm});
            skLineSegment(sketch, "E36.5.0.11", {"start": v(46.64, 12.38) * mm, "end": v(46.64, 17.71) * mm});
            skLineSegment(sketch, "E36.6.0.0", {"start": v(51.09, -17.71) * mm, "end": v(91.09, -17.71) * mm});
            skLineSegment(sketch, "E36.6.0.1", {"start": v(51.09, 7.05) * mm, "end": v(51.09, -17.71) * mm});
            skLineSegment(sketch, "E36.6.0.2", {"start": v(91.09, 7.05) * mm, "end": v(91.09, -17.71) * mm});
            skPoint(sketch, "E36.6.0.3", {"position": v(71.09, -5.33) * mm});
            skPoint(sketch, "E36.6.0.4", {"position": v(71.09, 7.05) * mm});
            skLineSegment(sketch, "E36.6.0.5", {"start": v(51.09, 7.05) * mm, "end": v(91.09, 7.05) * mm});
            skLineSegment(sketch, "E36.6.0.6", {"start": v(91.09, 12.38) * mm, "end": v(51.09, 12.38) * mm});
            skPoint(sketch, "E36.6.0.7", {"position": v(71.09, 15.05) * mm});
            skLineSegment(sketch, "E36.6.0.8", {"start": v(91.09, 17.71) * mm, "end": v(51.09, 17.71) * mm});
            skPoint(sketch, "E36.6.0.9", {"position": v(71.09, 7.05) * mm});
            skLineSegment(sketch, "E36.6.0.10", {"start": v(51.09, 12.38) * mm, "end": v(51.09, 17.71) * mm});
            skLineSegment(sketch, "E36.6.0.11", {"start": v(91.09, 12.38) * mm, "end": v(91.09, 17.71) * mm});
            skLineSegment(sketch, "E36.7.0.0", {"start": v(95.54, -17.71) * mm, "end": v(135.54, -17.71) * mm});
            skLineSegment(sketch, "E36.7.0.1", {"start": v(95.54, 7.05) * mm, "end": v(95.54, -17.71) * mm});
            skLineSegment(sketch, "E36.7.0.2", {"start": v(135.54, 7.05) * mm, "end": v(135.54, -17.71) * mm});
            skPoint(sketch, "E36.7.0.3", {"position": v(115.54, -5.33) * mm});
            skPoint(sketch, "E36.7.0.4", {"position": v(115.54, 7.05) * mm});
            skLineSegment(sketch, "E36.7.0.5", {"start": v(95.54, 7.05) * mm, "end": v(135.54, 7.05) * mm});
            skLineSegment(sketch, "E36.7.0.6", {"start": v(135.54, 12.38) * mm, "end": v(95.54, 12.38) * mm});
            skPoint(sketch, "E36.7.0.7", {"position": v(115.54, 15.05) * mm});
            skLineSegment(sketch, "E36.7.0.8", {"start": v(135.54, 17.71) * mm, "end": v(95.54, 17.71) * mm});
            skPoint(sketch, "E36.7.0.9", {"position": v(115.54, 7.05) * mm});
            skLineSegment(sketch, "E36.7.0.10", {"start": v(95.54, 12.38) * mm, "end": v(95.54, 17.71) * mm});
            skLineSegment(sketch, "E36.7.0.11", {"start": v(135.54, 12.38) * mm, "end": v(135.54, 17.71) * mm});
            skLineSegment(sketch, "E36.8.0.0", {"start": v(139.99, -17.71) * mm, "end": v(179.99, -17.71) * mm});
            skLineSegment(sketch, "E36.8.0.1", {"start": v(139.99, 7.05) * mm, "end": v(139.99, -17.71) * mm});
            skLineSegment(sketch, "E36.8.0.2", {"start": v(179.99, 7.05) * mm, "end": v(179.99, -17.71) * mm});
            skPoint(sketch, "E36.8.0.3", {"position": v(159.99, -5.33) * mm});
            skPoint(sketch, "E36.8.0.4", {"position": v(159.99, 7.05) * mm});
            skLineSegment(sketch, "E36.8.0.5", {"start": v(139.99, 7.05) * mm, "end": v(179.99, 7.05) * mm});
            skLineSegment(sketch, "E36.8.0.6", {"start": v(179.99, 12.38) * mm, "end": v(139.99, 12.38) * mm});
            skPoint(sketch, "E36.8.0.7", {"position": v(159.99, 15.05) * mm});
            skLineSegment(sketch, "E36.8.0.8", {"start": v(179.99, 17.71) * mm, "end": v(139.99, 17.71) * mm});
            skPoint(sketch, "E36.8.0.9", {"position": v(159.99, 7.05) * mm});
            skLineSegment(sketch, "E36.8.0.10", {"start": v(139.99, 12.38) * mm, "end": v(139.99, 17.71) * mm});
            skLineSegment(sketch, "E36.8.0.11", {"start": v(179.99, 12.38) * mm, "end": v(179.99, 17.71) * mm});
            skLineSegment(sketch, "E36.direction1", {"start": v(-215.61, -17.71) * mm, "end": v(-171.16, -17.71) * mm, "construction": true});
            skLineSegment(sketch, "E37.bottom", {"start": v(195.04, 12.7) * mm, "end": v(214.1, 12.7) * mm});
            skLineSegment(sketch, "E37.top", {"start": v(195.04, -12.7) * mm, "end": v(214.1, -12.7) * mm});
            skLineSegment(sketch, "E37.left", {"start": v(195.04, 12.7) * mm, "end": v(195.04, -12.7) * mm});
            skLineSegment(sketch, "E37.right", {"start": v(214.1, 12.7) * mm, "end": v(214.1, -12.7) * mm});
            skPoint(sketch, "E37.middle", {"position": v(204.57, 0) * mm});
            skSolve(sketch);
        }
        {
            var Q0;
            Q0 = qSketchRegion(id + "F11", true);
            extrude(context, id + "F12", {"entities" : qUnion([Q0]), "operationType" : NewBodyOperationType.ADD, "depth" : 1.27 * mm});
        }
        {
            var Q0;
            Q0=makeQuery(id+"F12.opExtrude","CAP_FACE",FACE,{"disambiguationData":[OSD([sQuery(id+"F11.wireOp",EDGE,"E36.1.0.0"),sQuery(id+"F11.wireOp",EDGE,"E36.1.0.1"),sQuery(id+"F11.wireOp",EDGE,"E36.1.0.2"),sQuery(id+"F11.wireOp",EDGE,"E36.1.0.5")])],"isStart":false});
            var sketch = newSketch(context, id + "F13", { "sketchPlane" : qUnion([Q0])});
            skLineSegment(sketch, "E38.bottom", {"start": v(-167.38, 1.9) * mm, "end": v(-159.76, 1.9) * mm});
            skLineSegment(sketch, "E38.top", {"start": v(-167.38, -1.9) * mm, "end": v(-159.76, -1.9) * mm});
            skLineSegment(sketch, "E38.left", {"start": v(-167.38, 1.9) * mm, "end": v(-167.38, -1.9) * mm});
            skLineSegment(sketch, "E38.right", {"start": v(-159.76, 1.9) * mm, "end": v(-159.76, -1.9) * mm});
            skPoint(sketch, "E38.middle", {"position": v(-163.57, 0) * mm});
            skLineSegment(sketch, "E39.bottom", {"start": v(-156, 1.9) * mm, "end": v(-148.39, 1.9) * mm});
            skLineSegment(sketch, "E39.top", {"start": v(-156, -1.9) * mm, "end": v(-148.39, -1.9) * mm});
            skLineSegment(sketch, "E39.left", {"start": v(-156, 1.9) * mm, "end": v(-156, -1.9) * mm});
            skLineSegment(sketch, "E39.right", {"start": v(-148.39, 1.9) * mm, "end": v(-148.39, -1.9) * mm});
            skPoint(sketch, "E39.middle", {"position": v(-152.2, 0) * mm});
            skCircle(sketch, "E40", {"center": v(-140.67, -9.06) * mm, "radius": 5.33 * mm});
            skCircle(sketch, "E41.1.0.0", {"center": v(-96.22, -9.06) * mm, "radius": 5.33 * mm});
            skLineSegment(sketch, "E41.1.0.1", {"start": v(-111.56, -1.9) * mm, "end": v(-103.94, -1.9) * mm});
            skPoint(sketch, "E41.1.0.2", {"position": v(-107.75, 0) * mm});
            skLineSegment(sketch, "E41.1.0.3", {"start": v(-122.93, 1.9) * mm, "end": v(-122.93, -1.9) * mm});
            skLineSegment(sketch, "E41.1.0.4", {"start": v(-111.56, 1.9) * mm, "end": v(-111.56, -1.9) * mm});
            skLineSegment(sketch, "E41.1.0.5", {"start": v(-103.94, 1.9) * mm, "end": v(-103.94, -1.9) * mm});
            skLineSegment(sketch, "E41.1.0.6", {"start": v(-122.93, -1.9) * mm, "end": v(-115.31, -1.9) * mm});
            skPoint(sketch, "E41.1.0.7", {"position": v(-119.12, 0) * mm});
            skLineSegment(sketch, "E41.1.0.8", {"start": v(-115.31, 1.9) * mm, "end": v(-115.31, -1.9) * mm});
            skLineSegment(sketch, "E41.1.0.9", {"start": v(-111.56, 1.9) * mm, "end": v(-103.94, 1.9) * mm});
            skLineSegment(sketch, "E41.1.0.10", {"start": v(-122.93, 1.9) * mm, "end": v(-115.31, 1.9) * mm});
            skCircle(sketch, "E41.2.0.0", {"center": v(-51.77, -9.06) * mm, "radius": 5.33 * mm});
            skLineSegment(sketch, "E41.2.0.1", {"start": v(-67.1, -1.9) * mm, "end": v(-59.49, -1.9) * mm});
            skPoint(sketch, "E41.2.0.2", {"position": v(-63.3, 0) * mm});
            skLineSegment(sketch, "E41.2.0.3", {"start": v(-78.48, 1.9) * mm, "end": v(-78.48, -1.9) * mm});
            skLineSegment(sketch, "E41.2.0.4", {"start": v(-67.1, 1.9) * mm, "end": v(-67.1, -1.9) * mm});
            skLineSegment(sketch, "E41.2.0.5", {"start": v(-59.49, 1.9) * mm, "end": v(-59.49, -1.9) * mm});
            skLineSegment(sketch, "E41.2.0.6", {"start": v(-78.48, -1.9) * mm, "end": v(-70.86, -1.9) * mm});
            skPoint(sketch, "E41.2.0.7", {"position": v(-74.67, 0) * mm});
            skLineSegment(sketch, "E41.2.0.8", {"start": v(-70.86, 1.9) * mm, "end": v(-70.86, -1.9) * mm});
            skLineSegment(sketch, "E41.2.0.9", {"start": v(-67.1, 1.9) * mm, "end": v(-59.49, 1.9) * mm});
            skLineSegment(sketch, "E41.2.0.10", {"start": v(-78.48, 1.9) * mm, "end": v(-70.86, 1.9) * mm});
            skCircle(sketch, "E41.3.0.0", {"center": v(-7.32, -9.06) * mm, "radius": 5.33 * mm});
            skLineSegment(sketch, "E41.3.0.1", {"start": v(-22.66, -1.9) * mm, "end": v(-15.04, -1.9) * mm});
            skPoint(sketch, "E41.3.0.2", {"position": v(-18.85, 0) * mm});
            skLineSegment(sketch, "E41.3.0.3", {"start": v(-34.03, 1.9) * mm, "end": v(-34.03, -1.9) * mm});
            skLineSegment(sketch, "E41.3.0.4", {"start": v(-22.66, 1.9) * mm, "end": v(-22.66, -1.9) * mm});
            skLineSegment(sketch, "E41.3.0.5", {"start": v(-15.04, 1.9) * mm, "end": v(-15.04, -1.9) * mm});
            skLineSegment(sketch, "E41.3.0.6", {"start": v(-34.03, -1.9) * mm, "end": v(-26.41, -1.9) * mm});
            skPoint(sketch, "E41.3.0.7", {"position": v(-30.22, 0) * mm});
            skLineSegment(sketch, "E41.3.0.8", {"start": v(-26.41, 1.9) * mm, "end": v(-26.41, -1.9) * mm});
            skLineSegment(sketch, "E41.3.0.9", {"start": v(-22.66, 1.9) * mm, "end": v(-15.04, 1.9) * mm});
            skLineSegment(sketch, "E41.3.0.10", {"start": v(-34.03, 1.9) * mm, "end": v(-26.41, 1.9) * mm});
            skCircle(sketch, "E41.4.0.0", {"center": v(37.13, -9.06) * mm, "radius": 5.33 * mm});
            skLineSegment(sketch, "E41.4.0.1", {"start": v(21.8, -1.9) * mm, "end": v(29.41, -1.9) * mm});
            skPoint(sketch, "E41.4.0.2", {"position": v(25.6, 0) * mm});
            skLineSegment(sketch, "E41.4.0.3", {"start": v(10.42, 1.9) * mm, "end": v(10.42, -1.9) * mm});
            skLineSegment(sketch, "E41.4.0.4", {"start": v(21.8, 1.9) * mm, "end": v(21.8, -1.9) * mm});
            skLineSegment(sketch, "E41.4.0.5", {"start": v(29.41, 1.9) * mm, "end": v(29.41, -1.9) * mm});
            skLineSegment(sketch, "E41.4.0.6", {"start": v(10.42, -1.9) * mm, "end": v(18.04, -1.9) * mm});
            skPoint(sketch, "E41.4.0.7", {"position": v(14.23, 0) * mm});
            skLineSegment(sketch, "E41.4.0.8", {"start": v(18.04, 1.9) * mm, "end": v(18.04, -1.9) * mm});
            skLineSegment(sketch, "E41.4.0.9", {"start": v(21.8, 1.9) * mm, "end": v(29.41, 1.9) * mm});
            skLineSegment(sketch, "E41.4.0.10", {"start": v(10.42, 1.9) * mm, "end": v(18.04, 1.9) * mm});
            skCircle(sketch, "E41.5.0.0", {"center": v(81.58, -9.06) * mm, "radius": 5.33 * mm});
            skLineSegment(sketch, "E41.5.0.1", {"start": v(66.24, -1.9) * mm, "end": v(73.86, -1.9) * mm});
            skPoint(sketch, "E41.5.0.2", {"position": v(70.05, 0) * mm});
            skLineSegment(sketch, "E41.5.0.3", {"start": v(54.87, 1.9) * mm, "end": v(54.87, -1.9) * mm});
            skLineSegment(sketch, "E41.5.0.4", {"start": v(66.24, 1.9) * mm, "end": v(66.24, -1.9) * mm});
            skLineSegment(sketch, "E41.5.0.5", {"start": v(73.86, 1.9) * mm, "end": v(73.86, -1.9) * mm});
            skLineSegment(sketch, "E41.5.0.6", {"start": v(54.87, -1.9) * mm, "end": v(62.49, -1.9) * mm});
            skPoint(sketch, "E41.5.0.7", {"position": v(58.68, 0) * mm});
            skLineSegment(sketch, "E41.5.0.8", {"start": v(62.49, 1.9) * mm, "end": v(62.49, -1.9) * mm});
            skLineSegment(sketch, "E41.5.0.9", {"start": v(66.24, 1.9) * mm, "end": v(73.86, 1.9) * mm});
            skLineSegment(sketch, "E41.5.0.10", {"start": v(54.87, 1.9) * mm, "end": v(62.49, 1.9) * mm});
            skCircle(sketch, "E41.6.0.0", {"center": v(126.03, -9.06) * mm, "radius": 5.33 * mm});
            skLineSegment(sketch, "E41.6.0.1", {"start": v(110.7, -1.9) * mm, "end": v(118.31, -1.9) * mm});
            skPoint(sketch, "E41.6.0.2", {"position": v(114.5, 0) * mm});
            skLineSegment(sketch, "E41.6.0.3", {"start": v(99.32, 1.9) * mm, "end": v(99.32, -1.9) * mm});
            skLineSegment(sketch, "E41.6.0.4", {"start": v(110.7, 1.9) * mm, "end": v(110.7, -1.9) * mm});
            skLineSegment(sketch, "E41.6.0.5", {"start": v(118.31, 1.9) * mm, "end": v(118.31, -1.9) * mm});
            skLineSegment(sketch, "E41.6.0.6", {"start": v(99.32, -1.9) * mm, "end": v(106.94, -1.9) * mm});
            skPoint(sketch, "E41.6.0.7", {"position": v(103.13, 0) * mm});
            skLineSegment(sketch, "E41.6.0.8", {"start": v(106.94, 1.9) * mm, "end": v(106.94, -1.9) * mm});
            skLineSegment(sketch, "E41.6.0.9", {"start": v(110.7, 1.9) * mm, "end": v(118.31, 1.9) * mm});
            skLineSegment(sketch, "E41.6.0.10", {"start": v(99.32, 1.9) * mm, "end": v(106.94, 1.9) * mm});
            skCircle(sketch, "E41.7.0.0", {"center": v(170.48, -9.06) * mm, "radius": 5.33 * mm});
            skLineSegment(sketch, "E41.7.0.1", {"start": v(155.14, -1.9) * mm, "end": v(162.76, -1.9) * mm});
            skPoint(sketch, "E41.7.0.2", {"position": v(158.95, 0) * mm});
            skLineSegment(sketch, "E41.7.0.3", {"start": v(143.77, 1.9) * mm, "end": v(143.77, -1.9) * mm});
            skLineSegment(sketch, "E41.7.0.4", {"start": v(155.14, 1.9) * mm, "end": v(155.14, -1.9) * mm});
            skLineSegment(sketch, "E41.7.0.5", {"start": v(162.76, 1.9) * mm, "end": v(162.76, -1.9) * mm});
            skLineSegment(sketch, "E41.7.0.6", {"start": v(143.77, -1.9) * mm, "end": v(151.39, -1.9) * mm});
            skPoint(sketch, "E41.7.0.7", {"position": v(147.58, 0) * mm});
            skLineSegment(sketch, "E41.7.0.8", {"start": v(151.39, 1.9) * mm, "end": v(151.39, -1.9) * mm});
            skLineSegment(sketch, "E41.7.0.9", {"start": v(155.14, 1.9) * mm, "end": v(162.76, 1.9) * mm});
            skLineSegment(sketch, "E41.7.0.10", {"start": v(143.77, 1.9) * mm, "end": v(151.39, 1.9) * mm});
            skLineSegment(sketch, "E41.direction1", {"start": v(-140.67, -9.06) * mm, "end": v(-96.22, -9.06) * mm, "construction": true});
            skSolve(sketch);
        }
        {
            var Q0;
            Q0 = qSketchRegion(id + "F13", true);
            extrude(context, id + "F14", {"entities" : qUnion([Q0]), "operationType" : NewBodyOperationType.ADD, "depth" : 9.52 * mm});
        }
        {
            var Q0;
            Q0=makeQuery(id+"F12.opExtrude","CAP_FACE",FACE,{"disambiguationData":[OSD([sQuery(id+"F11.wireOp",EDGE,"E34.bottom"),sQuery(id+"F11.wireOp",EDGE,"E34.top"),sQuery(id+"F11.wireOp",EDGE,"E34.left"),sQuery(id+"F11.wireOp",EDGE,"E34.right")])],"isStart":false});
            var sketch = newSketch(context, id + "F15", { "sketchPlane" : qUnion([Q0])});
            skCircle(sketch, "E42", {"center": v(-186.64, -9.9) * mm, "radius": 5.33 * mm});
            skCircle(sketch, "E43", {"center": v(-202.66, -9.9) * mm, "radius": 5.33 * mm});
            skSolve(sketch);
        }
        {
            var Q0;
            Q0 = qSketchRegion(id + "F15", true);
            extrude(context, id + "F16", {"entities" : qUnion([Q0]), "operationType" : NewBodyOperationType.ADD, "depth" : 9.52 * mm});
        }
        {
            var Q0;
            Q0=makeQuery(id+"F12.opExtrude","CAP_FACE",FACE,{"disambiguationData":[OSD([sQuery(id+"F11.wireOp",EDGE,"E37.bottom"),sQuery(id+"F11.wireOp",EDGE,"E37.top"),sQuery(id+"F11.wireOp",EDGE,"E37.left"),sQuery(id+"F11.wireOp",EDGE,"E37.right")])],"isStart":false});
            var sketch = newSketch(context, id + "F17", { "sketchPlane" : qUnion([Q0])});
            skLineSegment(sketch, "E44.bottom", {"start": v(198.22, 6.35) * mm, "end": v(210.92, 6.35) * mm});
            skLineSegment(sketch, "E44.top", {"start": v(198.22, -6.35) * mm, "end": v(210.92, -6.35) * mm});
            skLineSegment(sketch, "E44.left", {"start": v(198.22, 6.35) * mm, "end": v(198.22, -6.35) * mm});
            skLineSegment(sketch, "E44.right", {"start": v(210.92, 6.35) * mm, "end": v(210.92, -6.35) * mm});
            skPoint(sketch, "E44.middle", {"position": v(204.57, 0) * mm});
            skPoint(sketch, "E44.middle.positionSnap0", {"position": v(204.57, 12.7) * mm});
            skPoint(sketch, "E44.centerSnap0", {"position": v(204.57, 12.7) * mm});
            skSolve(sketch);
        }
        {
            var Q0;
            Q0 = qSketchRegion(id + "F17", true);
            extrude(context, id + "F18", {"entities" : qUnion([Q0]), "operationType" : NewBodyOperationType.ADD, "depth" : 5.08 * mm});
        }
    });
